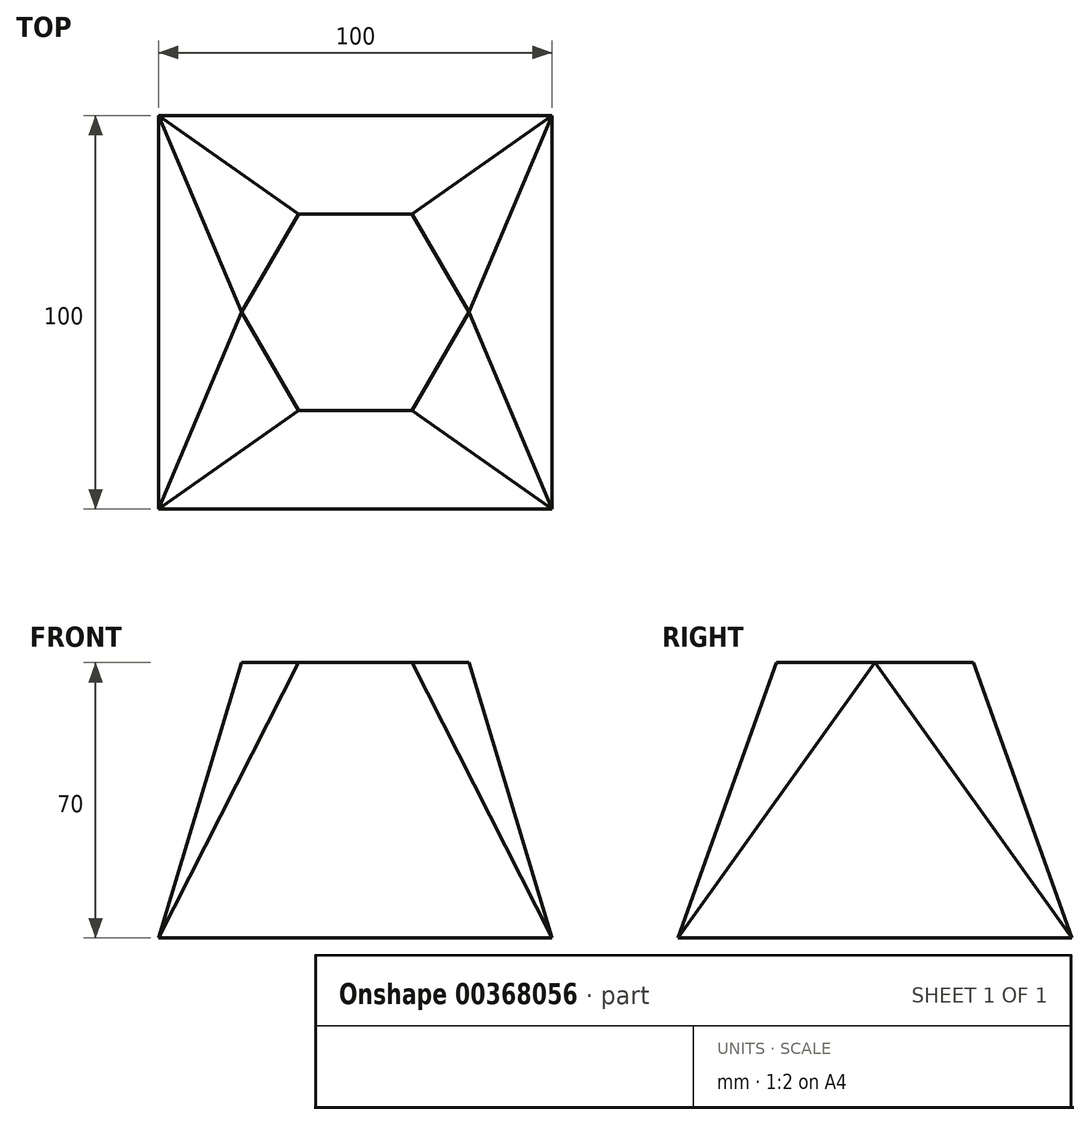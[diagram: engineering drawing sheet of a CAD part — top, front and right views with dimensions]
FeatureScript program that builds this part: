
annotation { "Feature Type Name" : "Feature", "Feature Type Description" : "" }
export const myFeature = defineFeature(function(context is Context, id is Id, definition is map)
    precondition{}
    {
        {
            var Q0;
            Q0=qCreatedBy(makeId("Top.planeOp"),FACE);
            var sketch = newSketch(context, id + "F0", { "sketchPlane" : qUnion([Q0])});
            skLineSegment(sketch, "E0.bottom", {"start": v(-50, 50) * mm, "end": v(50, 50) * mm});
            skLineSegment(sketch, "E0.top", {"start": v(-50, -50) * mm, "end": v(50, -50) * mm});
            skLineSegment(sketch, "E0.left", {"start": v(-50, 50) * mm, "end": v(-50, -50) * mm});
            skLineSegment(sketch, "E0.right", {"start": v(50, 50) * mm, "end": v(50, -50) * mm});
            skPoint(sketch, "E0.middle", {"position": v(0, 0) * mm});
            skSolve(sketch);
        }
        {
            var Q0;
            Q0=qCreatedBy(makeId("Top.planeOp"),FACE);
            cPlane(context, id + "F1", {"entities" : qUnion([Q0]), "cplaneType" : CPlaneType.OFFSET, "offset" : 70 * mm, "width" : 150 * mm, "height" : 150 * mm});
        }
        {
            var Q0;
            Q0=qCreatedBy(id+"F1.planeOp",FACE);
            var sketch = newSketch(context, id + "F2", { "sketchPlane" : qUnion([Q0])});
            skCircle(sketch, "E1.cCircle", {"center": v(0, 0) * mm, "radius": 25 * mm, "construction": true});
            skLineSegment(sketch, "E1.0", {"start": v(-14.43, 25) * mm, "end": v(14.43, 25) * mm});
            skLineSegment(sketch, "E1.1", {"start": v(14.43, 25) * mm, "end": v(28.87, 0) * mm});
            skLineSegment(sketch, "E1.2", {"start": v(28.87, 0) * mm, "end": v(14.43, -25) * mm});
            skLineSegment(sketch, "E1.3", {"start": v(14.43, -25) * mm, "end": v(-14.43, -25) * mm});
            skLineSegment(sketch, "E1.4", {"start": v(-14.43, -25) * mm, "end": v(-28.87, 0) * mm});
            skLineSegment(sketch, "E1.5", {"start": v(-28.87, 0) * mm, "end": v(-14.43, 25) * mm});
            skPoint(sketch, "E1.0.midPoint", {"position": v(0, 25) * mm});
            skLineSegment(sketch, "E2", {"start": v(-14.43, 25) * mm, "end": v(-14.43, -25) * mm});
            skLineSegment(sketch, "E3", {"start": v(14.43, 25) * mm, "end": v(14.43, -25) * mm});
            skSolve(sketch);
        }
        {
            var Q0;
            Q0=makeQuery(id+"F2.imprint","IMPRINT",FACE,{"disambiguationData":[TD([[makeQuery(id+"F2.imprint","IMPRINT",EDGE,{"derivedFrom":sQuery(id+"F2.wireOp",EDGE,"E1.0")}),-1.0]])]});
            var Q1;
            Q1=makeQuery(id+"F0.imprint","IMPRINT",FACE,{"disambiguationData":[TD([[makeQuery(id+"F0.imprint","IMPRINT",EDGE,{"derivedFrom":sQuery(id+"F0.wireOp",EDGE,"E0.bottom")}),-1.0]])]});
            loft(context, id + "F3", {"sheetProfilesArray" : [{ "sheetProfileEntities" : qUnion([Q0]) }, { "sheetProfileEntities" : qUnion([Q1]) }]});
        }
        {
            var Q1;
            Q1=makeQuery(id+"F2.imprint","IMPRINT",FACE,{"disambiguationData":[TD([[makeQuery(id+"F2.imprint","IMPRINT",EDGE,{"derivedFrom":sQuery(id+"F2.wireOp",EDGE,"E1.1")}),-1.0]])]});
            var Q2;
            Q2=sQuery(id+"F0.wireOp",VERTEX,"E0.top.end");
            loft(context, id + "F4", {"operationType" : NewBodyOperationType.ADD, "sheetProfilesArray" : [{ "sheetProfileEntities" : qUnion([Q1]) }, { "sheetProfileEntities" : qUnion([Q2]) }]});
        }
        {
            var Q1;
            Q1=makeQuery(id+"F2.imprint","IMPRINT",FACE,{"disambiguationData":[TD([[makeQuery(id+"F2.imprint","IMPRINT",EDGE,{"derivedFrom":sQuery(id+"F2.wireOp",EDGE,"E1.1")}),-1.0]])]});
            var Q2;
            Q2=sQuery(id+"F0.wireOp",VERTEX,"E0.right.start");
            loft(context, id + "F5", {"operationType" : NewBodyOperationType.ADD, "sheetProfilesArray" : [{ "sheetProfileEntities" : qUnion([Q1]) }, { "sheetProfileEntities" : qUnion([Q2]) }]});
        }
        {
            var Q1;
            Q1=makeQuery(id+"F5.opLoft","SWEPT_FACE",FACE,{"disambiguationData":[OSD([sQuery(id+"F2.wireOp",EDGE,"E1.1"),sQuery(id+"F2.wireOp",EDGE,"E1.2"),sQuery(id+"F2.wireOp",EDGE,"E1.3"),sQuery(id+"F2.wireOp",EDGE,"E3")])]});
            var Q2;
            Q2=makeQuery(id+"F4.opLoft","SWEPT_FACE",FACE,{"disambiguationData":[OSD([sQuery(id+"F2.wireOp",EDGE,"E1.0"),sQuery(id+"F2.wireOp",EDGE,"E1.1"),sQuery(id+"F2.wireOp",EDGE,"E1.2"),sQuery(id+"F2.wireOp",EDGE,"E3")])]});
            var Q3;
            Q3=sQuery(id+"F0.wireOp",VERTEX,"E0.right.start");
            var Q4;
            Q4=sQuery(id+"F0.wireOp",VERTEX,"E0.right.end");
            loft(context, id + "F6", {"operationType" : NewBodyOperationType.ADD, "sheetProfilesArray" : [{ "sheetProfileEntities" : qUnion([Q1]) }, { "sheetProfileEntities" : qUnion([Q2]) }], "matchConnections" : true, "connections" : [{ "connectionEntities" : qUnion([Q3, Q4]), "connectionEdgeQueries" : qUnion([]), "connectionEdgeParameters" : [] }]});
        }
        {
            var Q1;
            Q1=makeQuery(id+"F2.imprint","IMPRINT",FACE,{"disambiguationData":[TD([[makeQuery(id+"F2.imprint","IMPRINT",EDGE,{"derivedFrom":sQuery(id+"F2.wireOp",EDGE,"E1.4")}),-1.0]])]});
            var Q2;
            Q2=sQuery(id+"F0.wireOp",VERTEX,"E0.left.start");
            loft(context, id + "F7", {"operationType" : NewBodyOperationType.ADD, "sheetProfilesArray" : [{ "sheetProfileEntities" : qUnion([Q1]) }, { "sheetProfileEntities" : qUnion([Q2]) }]});
        }
        {
            var Q1;
            Q1=makeQuery(id+"F2.imprint","IMPRINT",FACE,{"disambiguationData":[TD([[makeQuery(id+"F2.imprint","IMPRINT",EDGE,{"derivedFrom":sQuery(id+"F2.wireOp",EDGE,"E1.4")}),-1.0]])]});
            var Q2;
            Q2=sQuery(id+"F0.wireOp",VERTEX,"E0.left.end");
            loft(context, id + "F8", {"operationType" : NewBodyOperationType.ADD, "sheetProfilesArray" : [{ "sheetProfileEntities" : qUnion([Q1]) }, { "sheetProfileEntities" : qUnion([Q2]) }]});
        }
        {
            var Q1;
            Q1=makeQuery(id+"F7.opLoft","SWEPT_FACE",FACE,{"disambiguationData":[OSD([sQuery(id+"F2.wireOp",EDGE,"E1.3"),sQuery(id+"F2.wireOp",EDGE,"E1.4"),sQuery(id+"F2.wireOp",EDGE,"E1.5"),sQuery(id+"F2.wireOp",EDGE,"E2")])]});
            var Q2;
            Q2=makeQuery(id+"F8.opLoft","SWEPT_FACE",FACE,{"disambiguationData":[OSD([sQuery(id+"F2.wireOp",EDGE,"E1.0"),sQuery(id+"F2.wireOp",EDGE,"E1.4"),sQuery(id+"F2.wireOp",EDGE,"E1.5"),sQuery(id+"F2.wireOp",EDGE,"E2")])]});
            var Q3;
            Q3=sQuery(id+"F0.wireOp",VERTEX,"E0.left.start");
            var Q4;
            Q4=sQuery(id+"F0.wireOp",VERTEX,"E0.left.end");
            loft(context, id + "F9", {"operationType" : NewBodyOperationType.ADD, "sheetProfilesArray" : [{ "sheetProfileEntities" : qUnion([Q1]) }, { "sheetProfileEntities" : qUnion([Q2]) }], "matchConnections" : true, "connections" : [{ "connectionEntities" : qUnion([Q3, Q4]), "connectionEdgeQueries" : qUnion([]), "connectionEdgeParameters" : [] }]});
        }
    });
